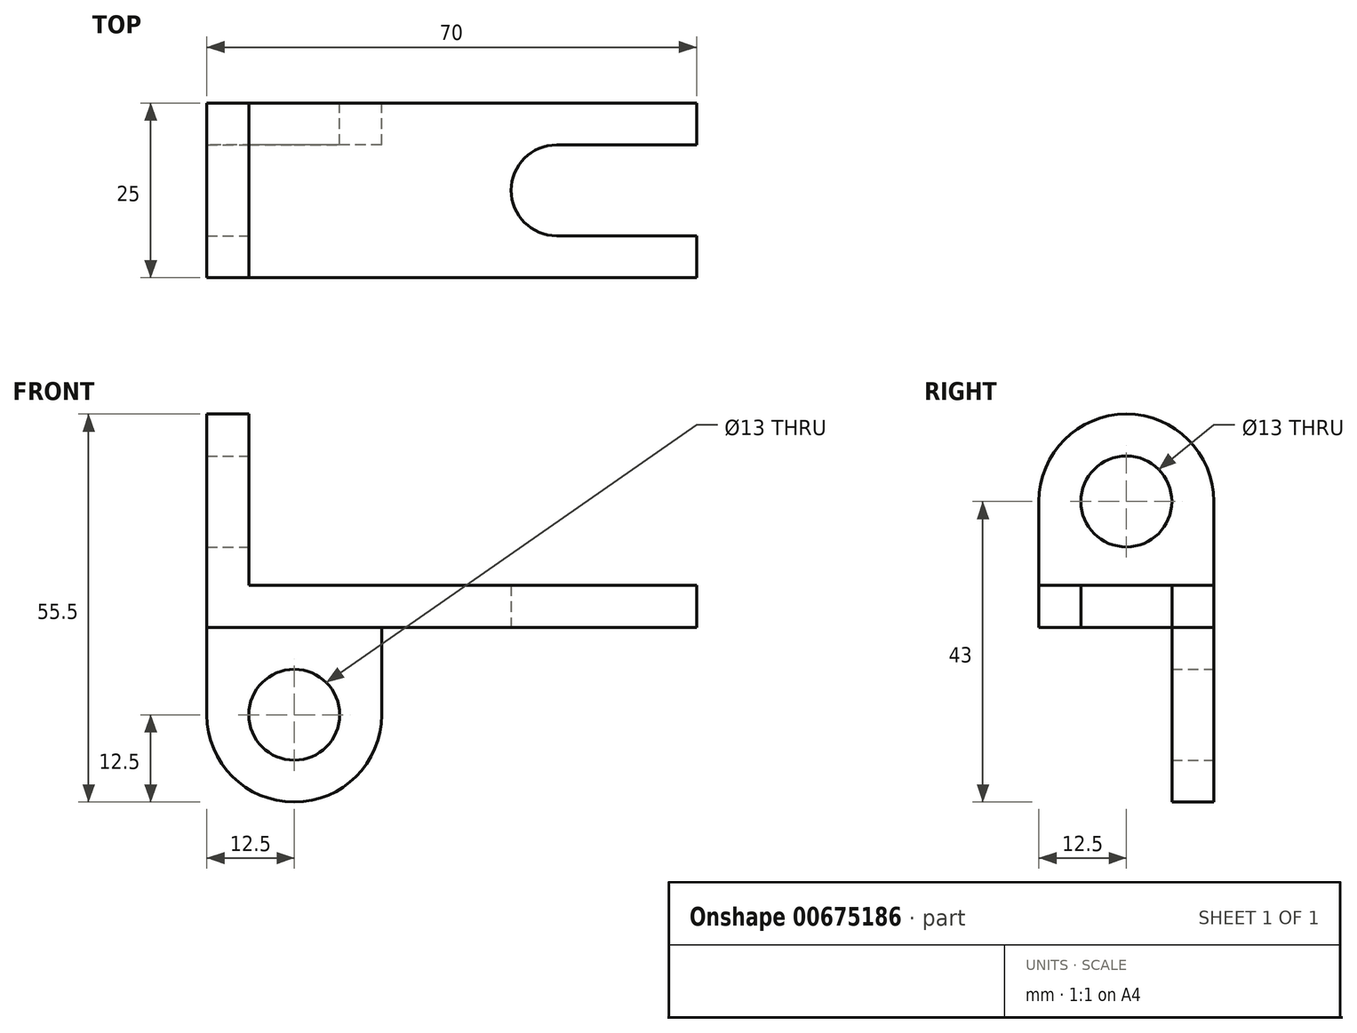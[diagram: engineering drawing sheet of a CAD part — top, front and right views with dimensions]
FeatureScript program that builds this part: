
annotation { "Feature Type Name" : "Feature", "Feature Type Description" : "" }
export const myFeature = defineFeature(function(context is Context, id is Id, definition is map)
    precondition{}
    {
        {
            var Q0;
            Q0=qCreatedBy(makeId("Top.planeOp"),FACE);
            var sketch = newSketch(context, id + "F0", { "sketchPlane" : qUnion([Q0])});
            skLineSegment(sketch, "E0.bottom", {"start": v(32, -12.5) * mm, "end": v(-32, -12.5) * mm});
            skLineSegment(sketch, "E0.top", {"start": v(32, 12.5) * mm, "end": v(-32, 12.5) * mm});
            skLineSegment(sketch, "E0.left", {"start": v(32, -12.5) * mm, "end": v(32, 12.5) * mm});
            skLineSegment(sketch, "E0.right", {"start": v(-32, -12.5) * mm, "end": v(-32, 12.5) * mm});
            skPoint(sketch, "E0.middle", {"position": v(0, 0) * mm});
            skLineSegment(sketch, "E1.bottom", {"start": v(32, -6.5) * mm, "end": v(12, -6.5) * mm});
            skLineSegment(sketch, "E1.top", {"start": v(32, 6.5) * mm, "end": v(12, 6.5) * mm});
            skLineSegment(sketch, "E1.left", {"start": v(32, -6.5) * mm, "end": v(32, 6.5) * mm});
            skLineSegment(sketch, "E1.right", {"start": v(12, -6.5) * mm, "end": v(12, 6.5) * mm});
            skPoint(sketch, "E1.middle", {"position": v(22, 0) * mm});
            skPoint(sketch, "E1.middle.positionSnap0", {"position": v(32, 0) * mm});
            skPoint(sketch, "E1.centerSnap0", {"position": v(32, 0) * mm});
            skCircle(sketch, "E2", {"center": v(12, 0) * mm, "radius": 6.5 * mm});
            skSolve(sketch);
        }
        {
            var Q0;
            {var subQ4=sQuery(id+"F0.wireOp",EDGE,"E0.bottom");Q0=makeQuery(id+"F0.imprint","IMPRINT",FACE,{"disambiguationData":[TD([[makeQuery(id+"F0.imprint","IMPRINT",EDGE,{"derivedFrom":subQ4}),-1.0]])]});}
            extrude(context, id + "F1", {"entities" : qUnion([Q0]), "depth" : 6 * mm, "offsetDistance" : 25 * mm});
        }
        {
            var Q0;
            Q0=makeQuery(id+"F1.opExtrude","SWEPT_FACE",FACE,{"disambiguationData":[OSD([sQuery(id+"F0.wireOp",EDGE,"E0.right")])]});
            var sketch = newSketch(context, id + "F2", { "sketchPlane" : qUnion([Q0])});
            skLineSegment(sketch, "E3.bottom", {"start": v(-12.5, 0) * mm, "end": v(12.5, 0) * mm});
            skLineSegment(sketch, "E3.left", {"start": v(-12.5, 0) * mm, "end": v(-12.5, 18) * mm});
            skLineSegment(sketch, "E3.right", {"start": v(12.5, 0) * mm, "end": v(12.5, 18) * mm});
            skArc(sketch, "E4", {"start": v(12.5, 18) * mm, "mid": v(0, 30.5) * mm, "end": v(-12.5, 18) * mm});
            skCircle(sketch, "E5", {"center": v(0, 18) * mm, "radius": 6.5 * mm});
            skSolve(sketch);
        }
        {
            var Q0;
            Q0 = qSketchRegion(id + "F2", true);
            extrude(context, id + "F3", {"entities" : qUnion([Q0]), "operationType" : NewBodyOperationType.ADD, "depth" : 6 * mm, "offsetDistance" : 25 * mm});
        }
        {
            var Q0;
            Q0=makeQuery(id+"F3.boolean.opBoolean","MERGE",FACE,{"derivedFrom":[makeQuery(id+"F1.opExtrude","SWEPT_FACE",FACE,{"disambiguationData":[OSD([sQuery(id+"F0.wireOp",EDGE,"E0.top")])]}),makeQuery(id+"F3.opExtrude","SWEPT_FACE",FACE,{"disambiguationData":[OSD([sQuery(id+"F2.wireOp",EDGE,"E3.left")])]})]});
            var sketch = newSketch(context, id + "F4", { "sketchPlane" : qUnion([Q0])});
            skLineSegment(sketch, "E6.bottom", {"start": v(38, 0) * mm, "end": v(13, 0) * mm});
            skLineSegment(sketch, "E6.left", {"start": v(38, 0) * mm, "end": v(38, -12.5) * mm});
            skLineSegment(sketch, "E6.right", {"start": v(13, 0) * mm, "end": v(13, -12.5) * mm});
            skArc(sketch, "E7", {"start": v(13, -12.5) * mm, "mid": v(25.5, -25) * mm, "end": v(38, -12.5) * mm});
            skCircle(sketch, "E8", {"center": v(25.5, -12.5) * mm, "radius": 6.5 * mm});
            skSolve(sketch);
        }
        {
            var Q0;
            Q0=makeQuery(id+"F4.imprint","IMPRINT",FACE,{"disambiguationData":[TD([[makeQuery(id+"F4.imprint","IMPRINT",EDGE,{"derivedFrom":sQuery(id+"F4.wireOp",EDGE,"E6.bottom")}),-1.0]])]});
            extrude(context, id + "F5", {"entities" : qUnion([Q0]), "operationType" : NewBodyOperationType.ADD, "oppositeDirection" : true, "depth" : 6 * mm, "offsetDistance" : 25 * mm});
        }
    });
